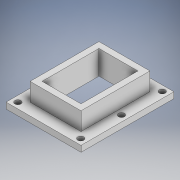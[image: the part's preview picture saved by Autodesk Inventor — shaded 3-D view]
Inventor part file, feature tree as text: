
AUTODESK INVENTOR PART (.ipt)
format: ipt  version: 2020 (Build 240168000, 168)  size: 148,992 bytes
history: native  units: mm
features: extrude x3, sketch x3, projected_geometry x1
ambient origin geometry x8: Origin, YZ Plane, XZ Plane, XY Plane, X Axis, Y Axis, Z Axis, Center Point
bodies: Solid1 (feature_tree)
feature tree (7):
  extrude  "Extrusion1"  Depth=19.0mm
  extrude  "Extrusion2"  Depth=23.0mm
  extrude  "Extrusion3"  Depth=25.0mm
  sketch  "Sketch1"  dims[d0=13.0mm d1=19.0mm]
  sketch  "Sketch2"  dims[d2=17.0mm d3=23.0mm]
  projected_geometry  "Projected Loop1"
  sketch  "Sketch3"  dims[d4=8.0mm d5=0.0mm d9=25.0mm d10=2.0mm d11=0.0mm d12=2.0mm d18=30.0mm d20=13.6mm d21=10.0mm d23=10.0mm d25=2.0mm d26=0.0mm]
